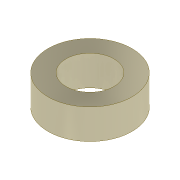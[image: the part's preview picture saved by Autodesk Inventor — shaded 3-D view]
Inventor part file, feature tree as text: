
AUTODESK INVENTOR PART (.ipt)
format: ipt  version: 2022 (Build 260153000, 153)  size: 90,112 bytes
history: native  units: mm
features: extrude x1, sketch x1
ambient origin geometry x8: Origin, YZ Plane, XZ Plane, XY Plane, X Axis, Y Axis, Z Axis, Center Point
bodies: Solid1 (feature_tree)
feature tree (2):
  extrude  "Extrusion1"  Depth=2.5mm
  sketch  "Sketch1"  dims[d0=4.0mm d1=7.0mm d2=2.5mm d3=0.0mm]
